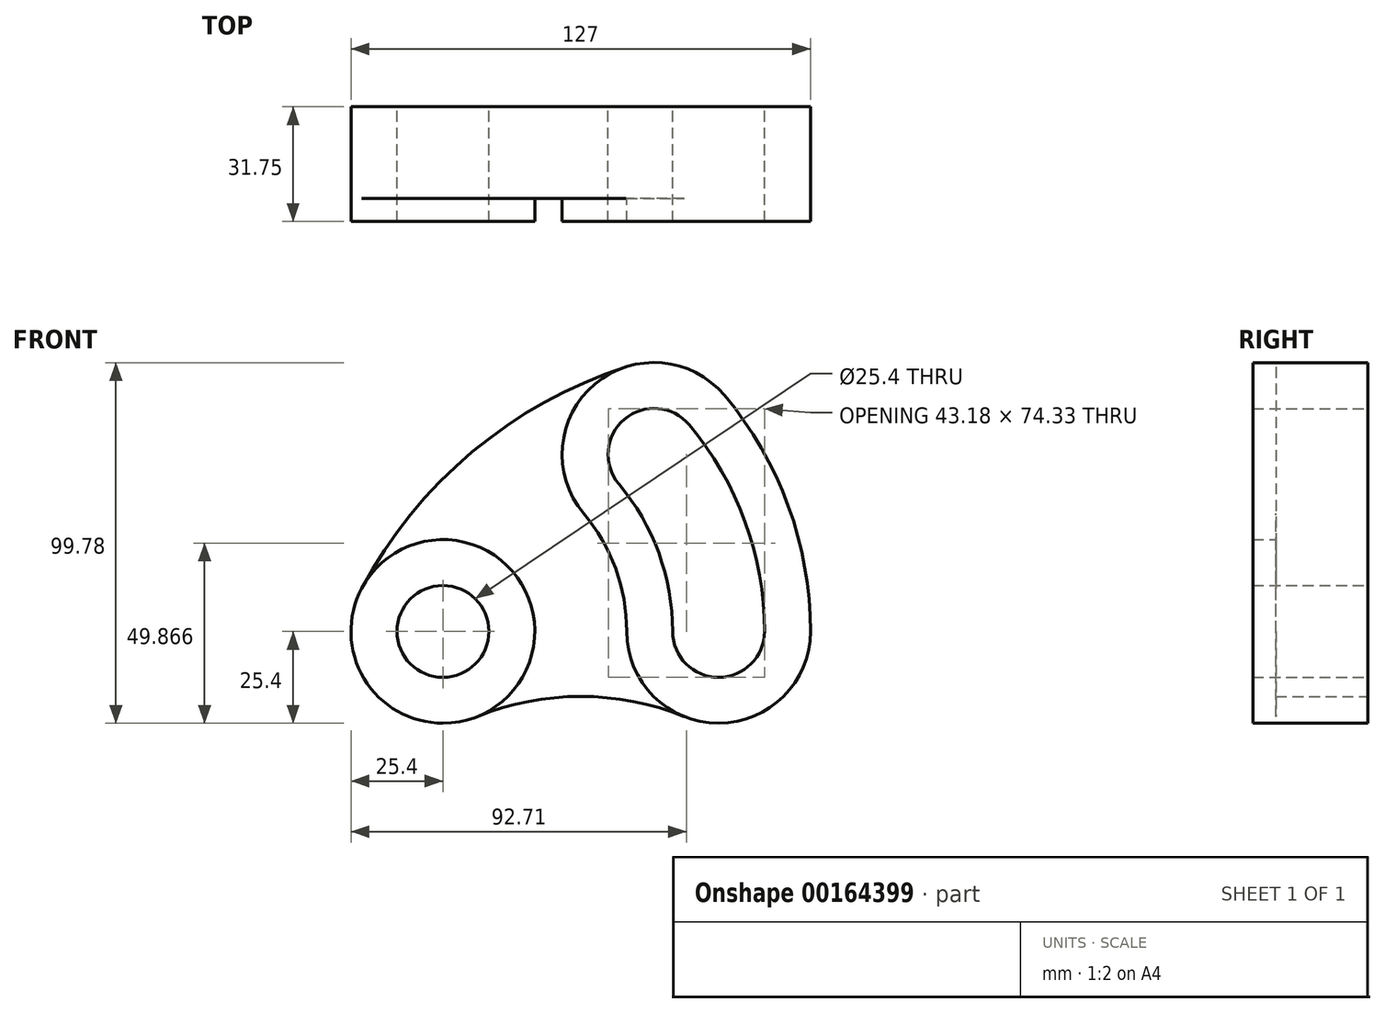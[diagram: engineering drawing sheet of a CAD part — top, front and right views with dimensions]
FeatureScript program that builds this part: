
annotation { "Feature Type Name" : "Feature", "Feature Type Description" : "" }
export const myFeature = defineFeature(function(context is Context, id is Id, definition is map)
    precondition{}
    {
        {
            var Q0;
            Q0=qCreatedBy(makeId("Front.planeOp"),FACE);
            var sketch = newSketch(context, id + "F0", { "sketchPlane" : qUnion([Q0])});
            skLineSegment(sketch, "E0", {"start": v(0, 0) * mm, "end": v(68.1, 57.14) * mm, "construction": true});
            skLineSegment(sketch, "E1", {"start": v(0, 0) * mm, "end": v(88.9, 0) * mm, "construction": true});
            skLineSegment(sketch, "E2", {"start": v(0, 21.75) * mm, "end": v(0, -22.73) * mm, "construction": true});
            skCircle(sketch, "E3", {"center": v(0, 0) * mm, "radius": 12.7 * mm});
            skCircle(sketch, "E4", {"center": v(0, 0) * mm, "radius": 25.4 * mm});
            skArc(sketch, "E5", {"start": v(64.18, -41.08) * mm, "mid": v(69.46, 31.34) * mm, "end": v(11.67, 75.3) * mm, "construction": true});
            skArc(sketch, "E6", {"start": v(63.5, 0) * mm, "mid": v(76.2, -12.7) * mm, "end": v(88.9, 0) * mm});
            skArc(sketch, "E7", {"start": v(88.9, 0) * mm, "mid": v(83.54, 30.4) * mm, "end": v(68.1, 57.14) * mm});
            skArc(sketch, "E8", {"start": v(63.5, 0) * mm, "mid": v(59.67, 21.72) * mm, "end": v(48.64, 40.82) * mm});
            skArc(sketch, "E9", {"start": v(68.1, 57.14) * mm, "mid": v(50.2, 58.7) * mm, "end": v(48.64, 40.82) * mm});
            skArc(sketch, "E10", {"start": v(50.8, 0) * mm, "mid": v(76.2, -25.4) * mm, "end": v(101.6, 0) * mm});
            skArc(sketch, "E11", {"start": v(101.6, 0) * mm, "mid": v(95.47, 34.75) * mm, "end": v(77.83, 65.3) * mm});
            skArc(sketch, "E12", {"start": v(77.83, 65.3) * mm, "mid": v(42.05, 68.44) * mm, "end": v(38.92, 32.65) * mm});
            skArc(sketch, "E13", {"start": v(50.8, 0) * mm, "mid": v(47.74, 17.37) * mm, "end": v(38.92, 32.65) * mm});
            skArc(sketch, "E14", {"start": v(50.53, 73.14) * mm, "mid": v(8.1, 49.63) * mm, "end": v(-22.43, 11.92) * mm});
            skArc(sketch, "E15", {"start": v(66.68, -23.55) * mm, "mid": v(38.1, -17.99) * mm, "end": v(9.52, -23.55) * mm});
            skSolve(sketch);
        }
        {
            var Q0;
            {var subQ0=sQuery(id+"F0.wireOp",EDGE,"E13");Q0=makeQuery(id+"F0.imprint","IMPRINT",FACE,{"disambiguationData":[TD([[makeQuery(id+"F0.imprint","IMPRINT",EDGE,{"derivedFrom":subQ0}),1.0]])]});}
            extrude(context, id + "F1", {"entities" : qUnion([Q0]), "depth" : 25.4 * mm});
        }
        {
            var Q0;
            Q0=makeQuery(id+"F0.imprint","IMPRINT",FACE,{"disambiguationData":[TD([[makeQuery(id+"F0.imprint","IMPRINT",EDGE,{"derivedFrom":sQuery(id+"F0.wireOp",EDGE,"E3")}),-1.0]])]});
            var Q1;
            Q1=makeQuery(id+"F0.imprint","IMPRINT",FACE,{"disambiguationData":[TD([[makeQuery(id+"F0.imprint","IMPRINT",EDGE,{"derivedFrom":sQuery(id+"F0.wireOp",EDGE,"E6")}),-1.0]])]});
            extrude(context, id + "F2", {"entities" : qUnion([Q0, Q1]), "operationType" : NewBodyOperationType.ADD, "depth" : 31.75 * mm});
        }
    });
